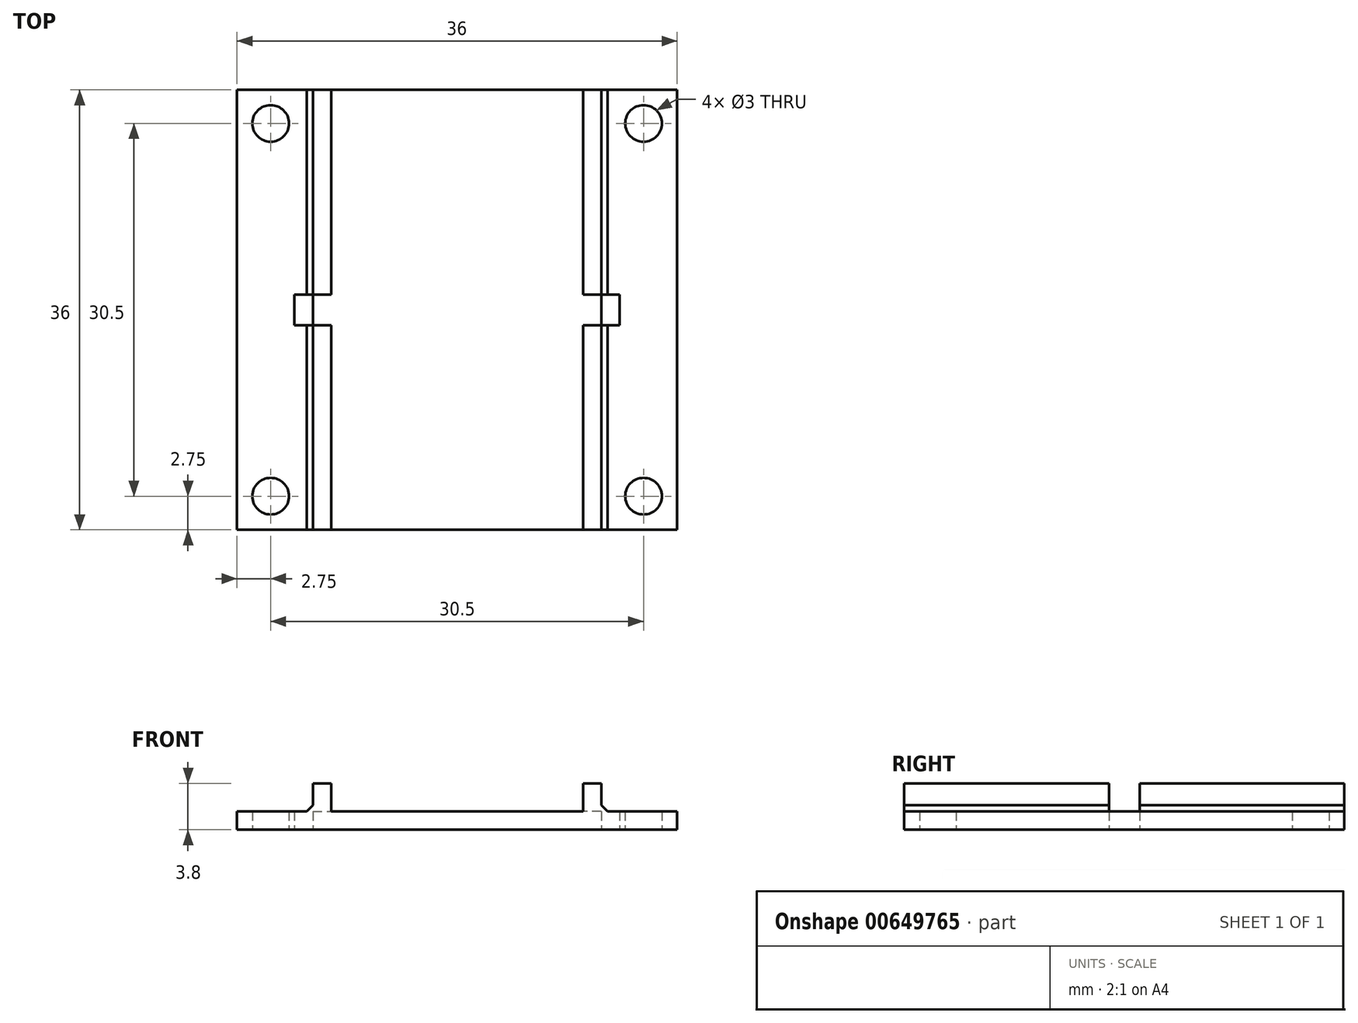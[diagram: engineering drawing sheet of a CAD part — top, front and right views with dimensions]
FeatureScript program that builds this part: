
annotation { "Feature Type Name" : "Feature", "Feature Type Description" : "" }
export const myFeature = defineFeature(function(context is Context, id is Id, definition is map)
    precondition{}
    {
        {
            var Q0;
            Q0=qCreatedBy(makeId("Top.planeOp"),FACE);
            var sketch = newSketch(context, id + "F0", { "sketchPlane" : qUnion([Q0])});
            skLineSegment(sketch, "E0.bottom", {"start": v(18, 18) * mm, "end": v(-18, 18) * mm});
            skLineSegment(sketch, "E0.top", {"start": v(18, -18) * mm, "end": v(-18, -18) * mm});
            skLineSegment(sketch, "E0.left", {"start": v(18, 18) * mm, "end": v(18, -18) * mm});
            skLineSegment(sketch, "E0.right", {"start": v(-18, 18) * mm, "end": v(-18, -18) * mm});
            skPoint(sketch, "E0.middle", {"position": v(0, 0) * mm});
            skLineSegment(sketch, "E1.bottom", {"start": v(15.25, 15.25) * mm, "end": v(-15.25, 15.25) * mm, "construction": true});
            skLineSegment(sketch, "E1.top", {"start": v(15.25, -15.25) * mm, "end": v(-15.25, -15.25) * mm, "construction": true});
            skLineSegment(sketch, "E1.left", {"start": v(15.25, 15.25) * mm, "end": v(15.25, -15.25) * mm, "construction": true});
            skLineSegment(sketch, "E1.right", {"start": v(-15.25, 15.25) * mm, "end": v(-15.25, -15.25) * mm, "construction": true});
            skCircle(sketch, "E2", {"center": v(-15.25, 15.25) * mm, "radius": 1.5 * mm});
            skCircle(sketch, "E3", {"center": v(15.25, 15.25) * mm, "radius": 1.5 * mm});
            skCircle(sketch, "E4", {"center": v(15.25, -15.25) * mm, "radius": 1.5 * mm});
            skCircle(sketch, "E5", {"center": v(-15.25, -15.25) * mm, "radius": 1.5 * mm});
            skLineSegment(sketch, "E6.bottom", {"start": v(-10.3, 18) * mm, "end": v(10.3, 18) * mm});
            skLineSegment(sketch, "E6.top", {"start": v(-10.3, -18) * mm, "end": v(10.3, -18) * mm});
            skLineSegment(sketch, "E6.left", {"start": v(-10.3, 18) * mm, "end": v(-10.3, -18) * mm});
            skLineSegment(sketch, "E6.right", {"start": v(10.3, 18) * mm, "end": v(10.3, -18) * mm});
            skLineSegment(sketch, "E7.bottom", {"start": v(-11.8, 18) * mm, "end": v(11.8, 18) * mm});
            skLineSegment(sketch, "E7.top", {"start": v(-11.8, -18) * mm, "end": v(11.8, -18) * mm});
            skLineSegment(sketch, "E7.left", {"start": v(-11.8, 18) * mm, "end": v(-11.8, -18) * mm});
            skLineSegment(sketch, "E7.right", {"start": v(11.8, 18) * mm, "end": v(11.8, -18) * mm});
            skPoint(sketch, "E8.centerSnap0", {"position": v(-15.25, 0) * mm});
            skPoint(sketch, "E9.centerSnap0", {"position": v(15.25, 0) * mm});
            skSolve(sketch);
        }
        {
            var Q0;
            {var subQ0=sQuery(id+"F0.wireOp",EDGE,"E0.right");Q0=makeQuery(id+"F0.imprint","IMPRINT",FACE,{"disambiguationData":[TD([[makeQuery(id+"F0.imprint","IMPRINT",EDGE,{"derivedFrom":subQ0}),1.0]])]});}
            var sketch = newSketch(context, id + "F1", { "sketchPlane" : qUnion([Q0])});
            skPoint(sketch, "E10.0", {"position": v(-10.3, 0) * mm});
            skPoint(sketch, "E11.0", {"position": v(-11.8, 0) * mm});
            skLineSegment(sketch, "E12", {"start": v(-11.8, 0) * mm, "end": v(-11.8, 1.25) * mm});
            skLineSegment(sketch, "E13", {"start": v(-11.8, 1.25) * mm, "end": v(-10.3, 1.25) * mm});
            skLineSegment(sketch, "E14", {"start": v(-10.3, 1.25) * mm, "end": v(-10.3, -1.25) * mm});
            skLineSegment(sketch, "E15", {"start": v(-10.3, -1.25) * mm, "end": v(-11.8, -1.25) * mm});
            skLineSegment(sketch, "E16", {"start": v(-11.8, -1.25) * mm, "end": v(-11.8, 0) * mm});
            skLineSegment(sketch, "E17.MirrorCS", {"start": v(11.8, 0) * mm, "end": v(11.8, 1.25) * mm});
            skLineSegment(sketch, "E18.MirrorCS", {"start": v(11.8, -1.25) * mm, "end": v(11.8, 0) * mm});
            skLineSegment(sketch, "E19.MirrorCS", {"start": v(10.3, 1.25) * mm, "end": v(10.3, -1.25) * mm});
            skLineSegment(sketch, "E20.MirrorCS", {"start": v(10.3, -1.25) * mm, "end": v(11.8, -1.25) * mm});
            skLineSegment(sketch, "E21.MirrorCS", {"start": v(11.8, 1.25) * mm, "end": v(10.3, 1.25) * mm});
            skPoint(sketch, "E22.MirrorP", {"position": v(10.3, 0) * mm});
            skPoint(sketch, "E23.MirrorP", {"position": v(11.8, 0) * mm});
            skSolve(sketch);
        }
        {
            var Q0;
            {var subQ0=sQuery(id+"F0.wireOp",EDGE,"E0.right");Q0=makeQuery(id+"F0.imprint","IMPRINT",FACE,{"disambiguationData":[TD([[makeQuery(id+"F0.imprint","IMPRINT",EDGE,{"derivedFrom":subQ0}),1.0]])]});}
            var sketch = newSketch(context, id + "F2", { "sketchPlane" : qUnion([Q0])});
            skPoint(sketch, "E24.0", {"position": v(-11.8, 1.25) * mm});
            skPoint(sketch, "E25.0", {"position": v(-11.8, -1.25) * mm});
            skLineSegment(sketch, "E26.bottom", {"start": v(-11.8, 1.25) * mm, "end": v(-13.3, 1.25) * mm});
            skLineSegment(sketch, "E26.top", {"start": v(-11.8, -1.25) * mm, "end": v(-13.3, -1.25) * mm});
            skLineSegment(sketch, "E26.left", {"start": v(-11.8, 1.25) * mm, "end": v(-11.8, -1.25) * mm});
            skLineSegment(sketch, "E26.right", {"start": v(-13.3, 1.25) * mm, "end": v(-13.3, -1.25) * mm});
            skLineSegment(sketch, "E27.MirrorCS", {"start": v(11.8, 1.25) * mm, "end": v(11.8, -1.25) * mm});
            skLineSegment(sketch, "E28.MirrorCS", {"start": v(11.8, 1.25) * mm, "end": v(13.3, 1.25) * mm});
            skLineSegment(sketch, "E29.MirrorCS", {"start": v(13.3, 1.25) * mm, "end": v(13.3, -1.25) * mm});
            skPoint(sketch, "E30.MirrorP", {"position": v(11.8, 1.25) * mm});
            skLineSegment(sketch, "E31.MirrorCS", {"start": v(11.8, -1.25) * mm, "end": v(13.3, -1.25) * mm});
            skPoint(sketch, "E32.MirrorP", {"position": v(11.8, -1.25) * mm});
            skSolve(sketch);
        }
        {
            var Q0;
            Q0 = qSketchRegion(id + "F0", true);
            extrude(context, id + "F3", {"entities" : qUnion([Q0]), "depth" : 1.5 * mm, "offsetDistance" : 25 * mm});
        }
        {
            var Q0;
            {var subQ0=sQuery(id+"F0.wireOp",EDGE,"E6.left");Q0=makeQuery(id+"F0.imprint","IMPRINT",FACE,{"disambiguationData":[TD([[makeQuery(id+"F0.imprint","IMPRINT",EDGE,{"derivedFrom":subQ0}),-1.0]])]});}
            var Q1;
            {var subQ0=sQuery(id+"F0.wireOp",EDGE,"E6.right");Q1=makeQuery(id+"F0.imprint","IMPRINT",FACE,{"disambiguationData":[TD([[makeQuery(id+"F0.imprint","IMPRINT",EDGE,{"derivedFrom":subQ0}),1.0]])]});}
            extrude(context, id + "F4", {"entities" : qUnion([Q0, Q1]), "operationType" : NewBodyOperationType.ADD, "depth" : 3.8 * mm, "offsetDistance" : 25 * mm});
        }
        {
            var Q0;
            Q0 = qSketchRegion(id + "F2", true);
            extrude(context, id + "F5", {"entities" : qUnion([Q0]), "operationType" : NewBodyOperationType.REMOVE, "depth" : 25 * mm, "offsetDistance" : 25 * mm});
        }
        {
            var Q0;
            {var subQ0=sQuery(id+"F0.wireOp",EDGE,"E7.bottom");var subQ1=sQuery(id+"F0.wireOp",EDGE,"E0.bottom");var subQ2=sQuery(id+"F0.wireOp",EDGE,"E7.left");var subQ3=makeQuery(id+"F3.opExtrude","CAP_FACE",FACE,{"disambiguationData":[OSD([subQ1,sQuery(id+"F0.wireOp",EDGE,"E0.top"),sQuery(id+"F0.wireOp",EDGE,"E0.left"),sQuery(id+"F0.wireOp",EDGE,"E0.right"),sQuery(id+"F0.wireOp",EDGE,"E2"),sQuery(id+"F0.wireOp",EDGE,"E3"),sQuery(id+"F0.wireOp",EDGE,"E4"),sQuery(id+"F0.wireOp",EDGE,"E5"),subQ0,sQuery(id+"F0.wireOp",EDGE,"E7.top")])],"isStart":false});var subQ4=makeQuery(id+"F4.opExtrude","SWEPT_FACE",FACE,{"disambiguationData":[OSD([subQ2])]});Q0=makeQuery(id+"F5.boolean.opBoolean","SPLIT",EDGE,{"disambiguationData":[TD([makeQuery(id+"F5.opExtrude","SWEPT_FACE",FACE,{"disambiguationData":[OSD([sQuery(id+"F2.wireOp",EDGE,"E26.bottom")])]})])],"derivedFrom":makeQuery(id+"F4.boolean.opBoolean","INTERSECT",EDGE,{"derivedFrom":[subQ3,subQ4]})});}
            var Q1;
            {var subQ0=sQuery(id+"F0.wireOp",EDGE,"E7.top");var subQ1=sQuery(id+"F0.wireOp",EDGE,"E0.top");var subQ2=sQuery(id+"F0.wireOp",EDGE,"E7.left");var subQ3=makeQuery(id+"F3.opExtrude","CAP_FACE",FACE,{"disambiguationData":[OSD([sQuery(id+"F0.wireOp",EDGE,"E0.bottom"),subQ1,sQuery(id+"F0.wireOp",EDGE,"E0.left"),sQuery(id+"F0.wireOp",EDGE,"E0.right"),sQuery(id+"F0.wireOp",EDGE,"E2"),sQuery(id+"F0.wireOp",EDGE,"E3"),sQuery(id+"F0.wireOp",EDGE,"E4"),sQuery(id+"F0.wireOp",EDGE,"E5"),sQuery(id+"F0.wireOp",EDGE,"E7.bottom"),subQ0])],"isStart":false});var subQ4=makeQuery(id+"F4.opExtrude","SWEPT_FACE",FACE,{"disambiguationData":[OSD([subQ2])]});Q1=makeQuery(id+"F5.boolean.opBoolean","SPLIT",EDGE,{"disambiguationData":[TD([makeQuery(id+"F5.opExtrude","SWEPT_FACE",FACE,{"disambiguationData":[OSD([sQuery(id+"F2.wireOp",EDGE,"E26.top")])]})])],"derivedFrom":makeQuery(id+"F4.boolean.opBoolean","INTERSECT",EDGE,{"derivedFrom":[subQ3,subQ4]})});}
            var Q2;
            {var subQ0=sQuery(id+"F0.wireOp",EDGE,"E7.top");var subQ1=sQuery(id+"F0.wireOp",EDGE,"E7.right");var subQ2=sQuery(id+"F0.wireOp",EDGE,"E0.top");var subQ3=makeQuery(id+"F3.opExtrude","CAP_FACE",FACE,{"disambiguationData":[OSD([sQuery(id+"F0.wireOp",EDGE,"E0.bottom"),subQ2,sQuery(id+"F0.wireOp",EDGE,"E0.left"),sQuery(id+"F0.wireOp",EDGE,"E0.right"),sQuery(id+"F0.wireOp",EDGE,"E2"),sQuery(id+"F0.wireOp",EDGE,"E3"),sQuery(id+"F0.wireOp",EDGE,"E4"),sQuery(id+"F0.wireOp",EDGE,"E5"),sQuery(id+"F0.wireOp",EDGE,"E7.bottom"),subQ0])],"isStart":false});var subQ4=makeQuery(id+"F4.opExtrude","SWEPT_FACE",FACE,{"disambiguationData":[OSD([subQ1])]});Q2=makeQuery(id+"F5.boolean.opBoolean","SPLIT",EDGE,{"disambiguationData":[TD([makeQuery(id+"F5.opExtrude","SWEPT_FACE",FACE,{"disambiguationData":[OSD([sQuery(id+"F2.wireOp",EDGE,"E31.MirrorCS")])]})])],"derivedFrom":makeQuery(id+"F4.boolean.opBoolean","INTERSECT",EDGE,{"derivedFrom":[subQ3,subQ4]})});}
            var Q3;
            {var subQ0=sQuery(id+"F0.wireOp",EDGE,"E7.bottom");var subQ1=sQuery(id+"F0.wireOp",EDGE,"E7.right");var subQ2=sQuery(id+"F0.wireOp",EDGE,"E0.bottom");var subQ3=makeQuery(id+"F3.opExtrude","CAP_FACE",FACE,{"disambiguationData":[OSD([subQ2,sQuery(id+"F0.wireOp",EDGE,"E0.top"),sQuery(id+"F0.wireOp",EDGE,"E0.left"),sQuery(id+"F0.wireOp",EDGE,"E0.right"),sQuery(id+"F0.wireOp",EDGE,"E2"),sQuery(id+"F0.wireOp",EDGE,"E3"),sQuery(id+"F0.wireOp",EDGE,"E4"),sQuery(id+"F0.wireOp",EDGE,"E5"),subQ0,sQuery(id+"F0.wireOp",EDGE,"E7.top")])],"isStart":false});var subQ4=makeQuery(id+"F4.opExtrude","SWEPT_FACE",FACE,{"disambiguationData":[OSD([subQ1])]});Q3=makeQuery(id+"F5.boolean.opBoolean","SPLIT",EDGE,{"disambiguationData":[TD([makeQuery(id+"F5.opExtrude","SWEPT_FACE",FACE,{"disambiguationData":[OSD([sQuery(id+"F2.wireOp",EDGE,"E28.MirrorCS")])]})])],"derivedFrom":makeQuery(id+"F4.boolean.opBoolean","INTERSECT",EDGE,{"derivedFrom":[subQ3,subQ4]})});}
            chamfer(context, id + "F6", {"entities" : qUnion([Q0, Q1, Q2, Q3]), "width" : .5 * mm, "tangentPropagation" : true});
        }
        {
            var Q0;
            {var subQ0=sQuery(id+"F0.wireOp",EDGE,"E2");var subQ1=sQuery(id+"F0.wireOp",EDGE,"E0.right");var subQ2=sQuery(id+"F0.wireOp",EDGE,"E7.top");var subQ3=sQuery(id+"F0.wireOp",EDGE,"E0.top");var subQ5=sQuery(id+"F0.wireOp",EDGE,"E7.bottom");var subQ6=sQuery(id+"F0.wireOp",EDGE,"E0.bottom");var subQ9=sQuery(id+"F0.wireOp",EDGE,"E5");Q0=makeQuery(id+"F4.boolean.opBoolean","SPLIT",FACE,{"disambiguationData":[TD([makeQuery(id+"F3.opExtrude","SWEPT_FACE",FACE,{"disambiguationData":[OSD([subQ1])]})])],"derivedFrom":makeQuery(id+"F3.opExtrude","CAP_FACE",FACE,{"disambiguationData":[OSD([subQ6,subQ3,sQuery(id+"F0.wireOp",EDGE,"E0.left"),subQ1,subQ0,sQuery(id+"F0.wireOp",EDGE,"E3"),sQuery(id+"F0.wireOp",EDGE,"E4"),subQ9,subQ5,subQ2])],"isStart":false})});}
            var sketch = newSketch(context, id + "F7", { "sketchPlane" : qUnion([Q0])});
            skPoint(sketch, "E33.0", {"position": v(-11.8, 1.25) * mm});
            skPoint(sketch, "E34.0", {"position": v(-10.3, -1.25) * mm});
            skLineSegment(sketch, "E35.bottom", {"start": v(-11.8, 1.25) * mm, "end": v(-10.3, 1.25) * mm});
            skLineSegment(sketch, "E35.top", {"start": v(-11.8, -1.25) * mm, "end": v(-10.3, -1.25) * mm});
            skLineSegment(sketch, "E35.left", {"start": v(-11.8, 1.25) * mm, "end": v(-11.8, -1.25) * mm});
            skLineSegment(sketch, "E35.right", {"start": v(-10.3, 1.25) * mm, "end": v(-10.3, -1.25) * mm});
            skLineSegment(sketch, "E36.MirrorCS", {"start": v(11.8, 1.25) * mm, "end": v(11.8, -1.25) * mm});
            skLineSegment(sketch, "E37.MirrorCS", {"start": v(10.3, 1.25) * mm, "end": v(10.3, -1.25) * mm});
            skPoint(sketch, "E38.MirrorP", {"position": v(11.8, 1.25) * mm});
            skPoint(sketch, "E39.MirrorP", {"position": v(10.3, -1.25) * mm});
            skLineSegment(sketch, "E40.MirrorCS", {"start": v(11.8, 1.25) * mm, "end": v(10.3, 1.25) * mm});
            skLineSegment(sketch, "E41.MirrorCS", {"start": v(11.8, -1.25) * mm, "end": v(10.3, -1.25) * mm});
            skSolve(sketch);
        }
        {
            var Q0;
            Q0 = qSketchRegion(id + "F7", true);
            extrude(context, id + "F8", {"entities" : qUnion([Q0]), "operationType" : NewBodyOperationType.REMOVE, "depth" : 25 * mm, "offsetDistance" : 25 * mm});
        }
    });
